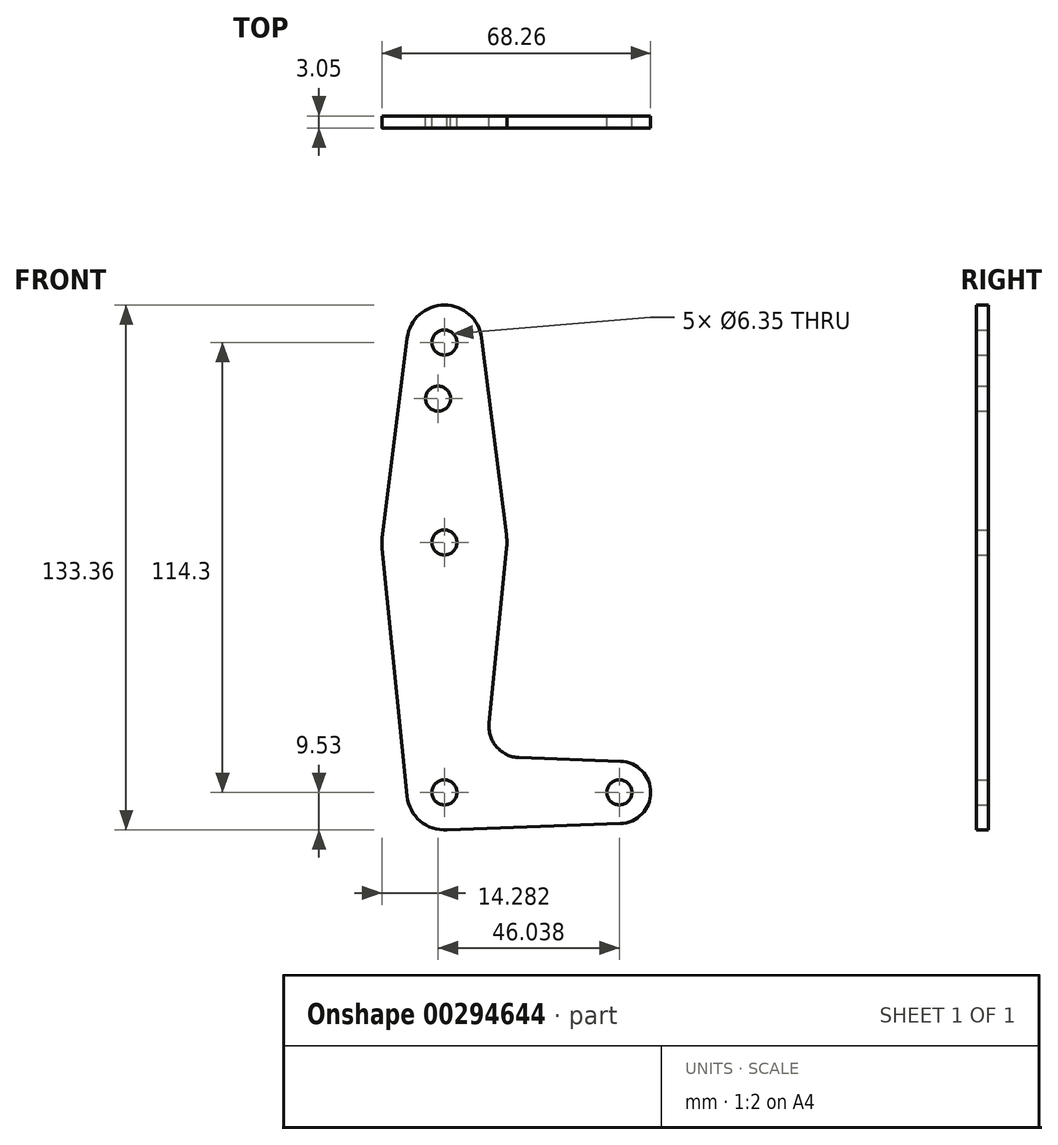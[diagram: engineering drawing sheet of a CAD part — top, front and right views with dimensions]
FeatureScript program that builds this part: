
annotation { "Feature Type Name" : "Feature", "Feature Type Description" : "" }
export const myFeature = defineFeature(function(context is Context, id is Id, definition is map)
    precondition{}
    {
        {
            var Q0;
            Q0=qCreatedBy(makeId("Front.planeOp"),FACE);
            var sketch = newSketch(context, id + "F0", { "sketchPlane" : qUnion([Q0])});
            skCircle(sketch, "E0", {"center": v(0, 0) * mm, "radius": 9.53 * mm});
            skCircle(sketch, "E1", {"center": v(44.45, 0) * mm, "radius": 7.94 * mm});
            skCircle(sketch, "E2", {"center": v(0, 63.5) * mm, "radius": 15.88 * mm});
            skCircle(sketch, "E3", {"center": v(0, 114.3) * mm, "radius": 9.53 * mm});
            skLineSegment(sketch, "E4", {"start": v(0, 114.3) * mm, "end": v(0, 63.5) * mm, "construction": true});
            skLineSegment(sketch, "E5", {"start": v(0, 63.5) * mm, "end": v(0, 0) * mm, "construction": true});
            skLineSegment(sketch, "E6", {"start": v(0, 0) * mm, "end": v(44.45, 0) * mm, "construction": true});
            skLineSegment(sketch, "E7", {"start": v(-9.45, 115.5) * mm, "end": v(-15.75, 65.48) * mm});
            skLineSegment(sketch, "E8", {"start": v(9.45, 115.5) * mm, "end": v(15.75, 65.48) * mm});
            skLineSegment(sketch, "E9", {"start": v(-15.8, 61.91) * mm, "end": v(-9.48, -0.95) * mm});
            skLineSegment(sketch, "E10", {"start": v(18.97, 8.85) * mm, "end": v(44.73, 7.93) * mm});
            skLineSegment(sketch, "E11", {"start": v(0, -9.52) * mm, "end": v(44.73, -7.93) * mm});
            skLineSegment(sketch, "E12", {"start": v(15.8, 61.91) * mm, "end": v(11.34, 17.59) * mm});
            skCircle(sketch, "E13", {"center": v(0, 114.3) * mm, "radius": 3.18 * mm});
            skCircle(sketch, "E14", {"center": v(0, 63.5) * mm, "radius": 3.18 * mm});
            skCircle(sketch, "E15", {"center": v(0, 0) * mm, "radius": 3.18 * mm});
            skCircle(sketch, "E16", {"center": v(44.45, 0) * mm, "radius": 3.18 * mm});
            skCircle(sketch, "E17", {"center": v(-1.59, 100.03) * mm, "radius": 3.18 * mm});
            skPoint(sketch, "E18.newPointA", {"position": v(9.57, 0) * mm});
            skArc(sketch, "E18.filletArc", {"start": v(11.34, 17.59) * mm, "mid": v(13.26, 11.57) * mm, "end": v(18.97, 8.85) * mm});
            skSolve(sketch);
        }
        {
            var Q0;
            Q0 = qSketchRegion(id + "F0", true);
            extrude(context, id + "F1", {"entities" : qUnion([Q0]), "depth" : 3.05 * mm});
        }
    });
